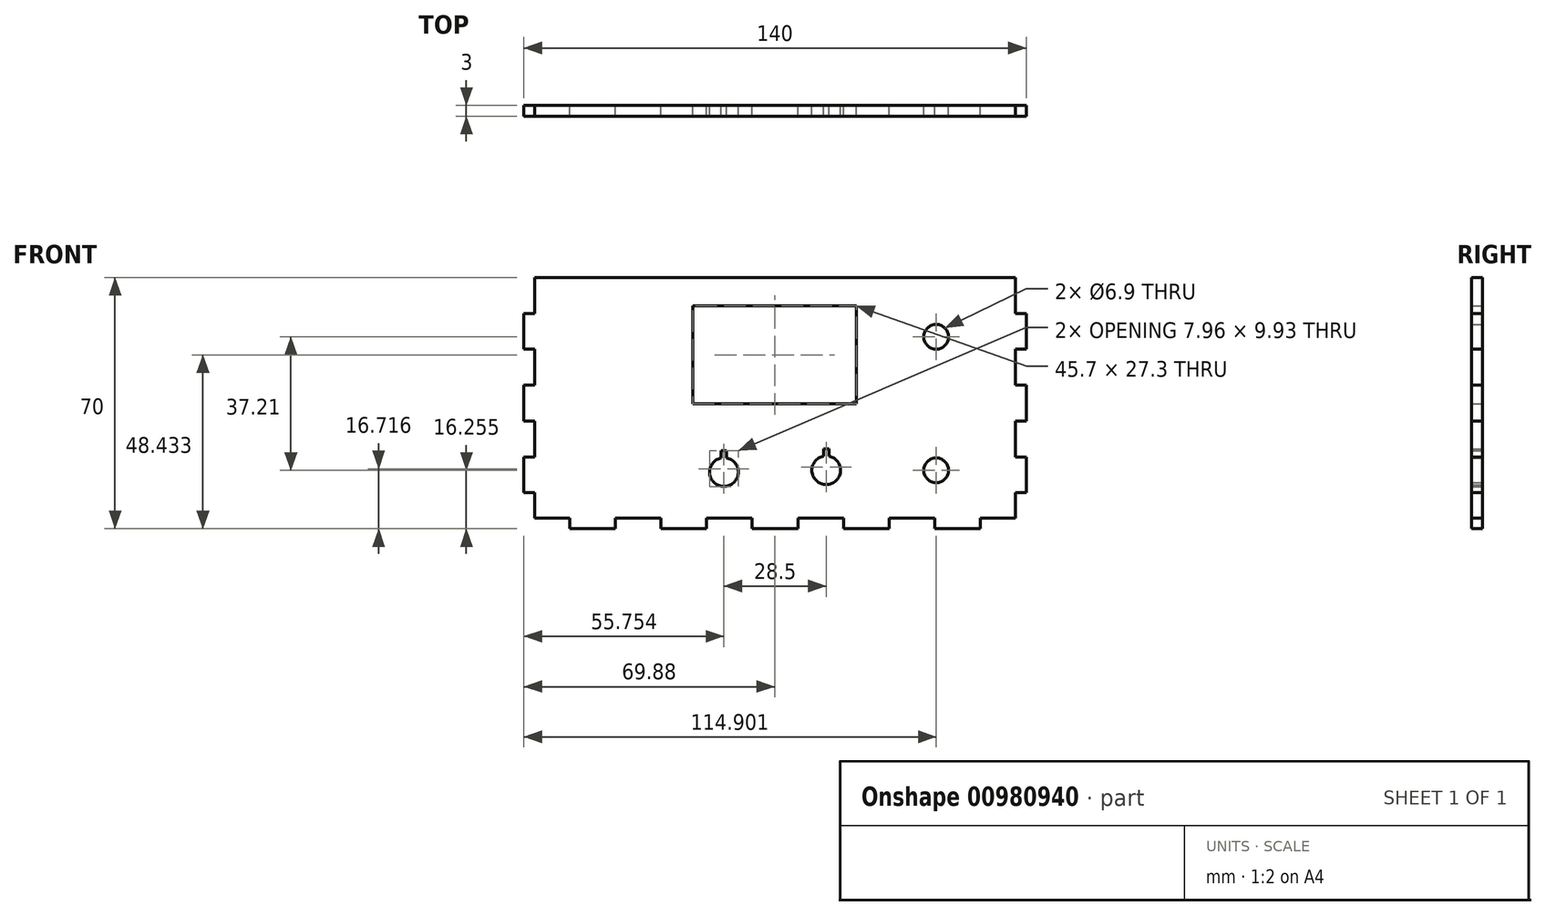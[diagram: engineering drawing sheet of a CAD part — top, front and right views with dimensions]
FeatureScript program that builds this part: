
annotation { "Feature Type Name" : "Feature", "Feature Type Description" : "" }
export const myFeature = defineFeature(function(context is Context, id is Id, definition is map)
    precondition{}
    {
        {
            var Q0;
            Q0=qCreatedBy(makeId("Front.planeOp"),FACE);
            var sketch = newSketch(context, id + "F0", { "sketchPlane" : qUnion([Q0])});
            skLineSegment(sketch, "E0.top", {"start": v(67.12, 35.14) * mm, "end": v(-66.88, 35.14) * mm});
            skPoint(sketch, "E0.middle", {"position": v(0.12, 0.14) * mm});
            skLineSegment(sketch, "E1", {"start": v(-66.88, -31.86) * mm, "end": v(-57.15, -31.86) * mm});
            skLineSegment(sketch, "E2", {"start": v(-57.15, -31.86) * mm, "end": v(-57.15, -34.86) * mm});
            skLineSegment(sketch, "E3", {"start": v(-57.15, -34.86) * mm, "end": v(-44.42, -34.86) * mm});
            skLineSegment(sketch, "E4", {"start": v(-44.42, -34.86) * mm, "end": v(-44.42, -31.86) * mm});
            skLineSegment(sketch, "E5", {"start": v(-44.42, -31.86) * mm, "end": v(-31.7, -31.86) * mm});
            skLineSegment(sketch, "E6.1.0.0", {"start": v(-18.97, -31.86) * mm, "end": v(-6.24, -31.86) * mm});
            skLineSegment(sketch, "E6.1.0.1", {"start": v(-31.7, -34.86) * mm, "end": v(-18.97, -34.86) * mm});
            skLineSegment(sketch, "E6.1.0.3", {"start": v(-18.97, -34.86) * mm, "end": v(-18.97, -31.86) * mm});
            skLineSegment(sketch, "E6.1.0.4", {"start": v(-31.7, -31.86) * mm, "end": v(-31.7, -34.86) * mm});
            skLineSegment(sketch, "E6.2.0.0", {"start": v(6.48, -31.86) * mm, "end": v(19.21, -31.86) * mm});
            skLineSegment(sketch, "E6.2.0.1", {"start": v(-6.24, -34.86) * mm, "end": v(6.48, -34.86) * mm});
            skLineSegment(sketch, "E6.2.0.2", {"start": v(-18.97, -31.86) * mm, "end": v(-6.24, -31.86) * mm});
            skLineSegment(sketch, "E6.2.0.3", {"start": v(6.48, -34.86) * mm, "end": v(6.48, -31.86) * mm});
            skLineSegment(sketch, "E6.2.0.4", {"start": v(-6.24, -31.86) * mm, "end": v(-6.24, -34.86) * mm});
            skLineSegment(sketch, "E6.3.0.0", {"start": v(31.94, -31.86) * mm, "end": v(44.67, -31.86) * mm});
            skLineSegment(sketch, "E6.3.0.1", {"start": v(19.21, -34.86) * mm, "end": v(31.94, -34.86) * mm});
            skLineSegment(sketch, "E6.3.0.2", {"start": v(6.48, -31.86) * mm, "end": v(19.21, -31.86) * mm});
            skLineSegment(sketch, "E6.3.0.3", {"start": v(31.94, -34.86) * mm, "end": v(31.94, -31.86) * mm});
            skLineSegment(sketch, "E6.3.0.4", {"start": v(19.21, -31.86) * mm, "end": v(19.21, -34.86) * mm});
            skLineSegment(sketch, "E6.4.0.0", {"start": v(57.4, -31.86) * mm, "end": v(67.12, -31.86) * mm});
            skLineSegment(sketch, "E6.4.0.1", {"start": v(44.67, -34.86) * mm, "end": v(57.4, -34.86) * mm});
            skLineSegment(sketch, "E6.4.0.2", {"start": v(31.94, -31.86) * mm, "end": v(44.67, -31.86) * mm});
            skLineSegment(sketch, "E6.4.0.3", {"start": v(57.4, -34.86) * mm, "end": v(57.4, -31.86) * mm});
            skLineSegment(sketch, "E6.4.0.4", {"start": v(44.67, -31.86) * mm, "end": v(44.67, -34.86) * mm});
            skLineSegment(sketch, "E6.direction1", {"start": v(-66.88, -31.86) * mm, "end": v(-44.42, -31.86) * mm, "construction": true});
            skLineSegment(sketch, "E7", {"start": v(-66.88, -31.86) * mm, "end": v(-66.88, -24.86) * mm});
            skLineSegment(sketch, "E8", {"start": v(-66.88, -24.86) * mm, "end": v(-69.88, -24.86) * mm});
            skLineSegment(sketch, "E9", {"start": v(-69.88, -24.86) * mm, "end": v(-69.88, -14.86) * mm});
            skLineSegment(sketch, "E10", {"start": v(-69.88, -14.86) * mm, "end": v(-66.88, -14.86) * mm});
            skPoint(sketch, "E0.right.start.orphan", {"position": v(-69.88, -34.86) * mm});
            skLineSegment(sketch, "E11.1.0.1", {"start": v(-69.88, -4.86) * mm, "end": v(-69.88, 5.14) * mm});
            skPoint(sketch, "E11.1.0.3", {"position": v(-69.88, -14.86) * mm});
            skLineSegment(sketch, "E11.1.0.4", {"start": v(-69.88, 5.14) * mm, "end": v(-66.88, 5.14) * mm});
            skLineSegment(sketch, "E11.1.0.5", {"start": v(-66.88, -4.86) * mm, "end": v(-69.88, -4.86) * mm});
            skLineSegment(sketch, "E11.2.0.1", {"start": v(-69.88, 15.14) * mm, "end": v(-69.88, 25.14) * mm});
            skLineSegment(sketch, "E11.2.0.2", {"start": v(-66.88, 25.14) * mm, "end": v(-66.88, 35.14) * mm});
            skPoint(sketch, "E11.2.0.3", {"position": v(-69.88, 5.14) * mm});
            skLineSegment(sketch, "E11.2.0.4", {"start": v(-69.88, 25.14) * mm, "end": v(-66.88, 25.14) * mm});
            skLineSegment(sketch, "E11.2.0.5", {"start": v(-66.88, 15.14) * mm, "end": v(-69.88, 15.14) * mm});
            skLineSegment(sketch, "E11.direction1", {"start": v(-66.88, -31.86) * mm, "end": v(-66.88, -14.86) * mm, "construction": true});
            skPoint(sketch, "E12.orphan", {"position": v(-66.88, -4.86) * mm});
            skPoint(sketch, "E13.orphan", {"position": v(-66.88, 15.14) * mm});
            skLineSegment(sketch, "E14", {"start": v(-66.88, -14.86) * mm, "end": v(-66.88, -4.86) * mm});
            skLineSegment(sketch, "E15", {"start": v(-66.88, 5.14) * mm, "end": v(-66.88, 15.14) * mm});
            skPoint(sketch, "E16.orphan", {"position": v(-69.88, 35.14) * mm});
            skPoint(sketch, "E17.orphan", {"position": v(-69.88, -31.86) * mm});
            skPoint(sketch, "E0.left.start.orphan", {"position": v(70.12, -34.86) * mm});
            skLineSegment(sketch, "E18.MirrorCS", {"start": v(67.12, -31.86) * mm, "end": v(67.12, -24.86) * mm});
            skLineSegment(sketch, "E19.MirrorCS", {"start": v(70.12, 25.14) * mm, "end": v(67.12, 25.14) * mm});
            skLineSegment(sketch, "E20.MirrorCS", {"start": v(70.12, -24.86) * mm, "end": v(70.12, -14.86) * mm});
            skPoint(sketch, "E21.MirrorP", {"position": v(70.12, 5.14) * mm});
            skPoint(sketch, "E22.MirrorP", {"position": v(70.12, 35.14) * mm});
            skLineSegment(sketch, "E23.MirrorCS", {"start": v(70.12, -14.86) * mm, "end": v(67.12, -14.86) * mm});
            skLineSegment(sketch, "E24.MirrorCS", {"start": v(67.12, 5.14) * mm, "end": v(67.12, 15.14) * mm});
            skLineSegment(sketch, "E25.MirrorCS", {"start": v(67.12, 25.14) * mm, "end": v(67.12, 35.14) * mm});
            skLineSegment(sketch, "E26.MirrorCS", {"start": v(70.12, 15.14) * mm, "end": v(70.12, 25.14) * mm});
            skLineSegment(sketch, "E27.MirrorCS", {"start": v(67.12, -4.86) * mm, "end": v(70.12, -4.86) * mm});
            skPoint(sketch, "E28.MirrorP", {"position": v(70.12, -31.86) * mm});
            skPoint(sketch, "E29.MirrorP", {"position": v(67.12, 15.14) * mm});
            skPoint(sketch, "E30.MirrorP", {"position": v(67.12, -4.86) * mm});
            skLineSegment(sketch, "E31.MirrorCS", {"start": v(67.12, -31.86) * mm, "end": v(67.12, -14.86) * mm, "construction": true});
            skLineSegment(sketch, "E32.MirrorCS", {"start": v(70.12, 5.14) * mm, "end": v(67.12, 5.14) * mm});
            skLineSegment(sketch, "E33.MirrorCS", {"start": v(70.12, -4.86) * mm, "end": v(70.12, 5.14) * mm});
            skLineSegment(sketch, "E34.MirrorCS", {"start": v(67.12, 15.14) * mm, "end": v(70.12, 15.14) * mm});
            skPoint(sketch, "E35.MirrorP", {"position": v(70.12, -14.86) * mm});
            skLineSegment(sketch, "E36.MirrorCS", {"start": v(67.12, -14.86) * mm, "end": v(67.12, -4.86) * mm});
            skLineSegment(sketch, "E37.MirrorCS", {"start": v(67.12, -24.86) * mm, "end": v(70.12, -24.86) * mm});
            skLineSegment(sketch, "E38.bottom", {"start": v(22.85, -0.08) * mm, "end": v(-22.85, -0.08) * mm});
            skLineSegment(sketch, "E38.top", {"start": v(22.85, 27.22) * mm, "end": v(-22.85, 27.22) * mm});
            skLineSegment(sketch, "E38.left", {"start": v(22.85, -0.08) * mm, "end": v(22.85, 27.22) * mm});
            skLineSegment(sketch, "E38.right", {"start": v(-22.85, -0.08) * mm, "end": v(-22.85, 27.22) * mm});
            skPoint(sketch, "E38.middle", {"position": v(0, 13.57) * mm});
            skCircle(sketch, "E39", {"center": v(45.02, -18.6) * mm, "radius": 3.45 * mm});
            skArc(sketch, "E40", {"start": v(-14.88, -15.18) * mm, "mid": v(-14.13, -23.1) * mm, "end": v(-13.38, -15.18) * mm});
            skArc(sketch, "E41", {"start": v(13.62, -14.68) * mm, "mid": v(14.37, -22.6) * mm, "end": v(15.12, -14.68) * mm});
            skLineSegment(sketch, "E42", {"start": v(-14.88, -15.18) * mm, "end": v(-14.88, -13.18) * mm});
            skLineSegment(sketch, "E43", {"start": v(-14.88, -13.18) * mm, "end": v(-13.38, -13.18) * mm});
            skLineSegment(sketch, "E44", {"start": v(-13.38, -13.18) * mm, "end": v(-13.38, -15.18) * mm});
            skLineSegment(sketch, "E45", {"start": v(13.62, -14.68) * mm, "end": v(13.62, -12.68) * mm});
            skLineSegment(sketch, "E46", {"start": v(13.62, -12.68) * mm, "end": v(15.12, -12.68) * mm});
            skLineSegment(sketch, "E47", {"start": v(15.12, -12.68) * mm, "end": v(15.12, -14.68) * mm});
            skCircle(sketch, "E48.MirrorC", {"center": v(45.02, 18.6) * mm, "radius": 3.45 * mm});
            skSolve(sketch);
        }
        {
            var Q0;
            Q0=makeQuery(id+"F0.imprint","IMPRINT",FACE,{"disambiguationData":[TD([[makeQuery(id+"F0.imprint","IMPRINT",EDGE,{"derivedFrom":sQuery(id+"F0.wireOp",EDGE,"E0.top")}),1.0]])]});
            extrude(context, id + "F1", {"entities" : qUnion([Q0]), "depth" : 3 * mm, "offsetDistance" : 25 * mm});
        }
    });
